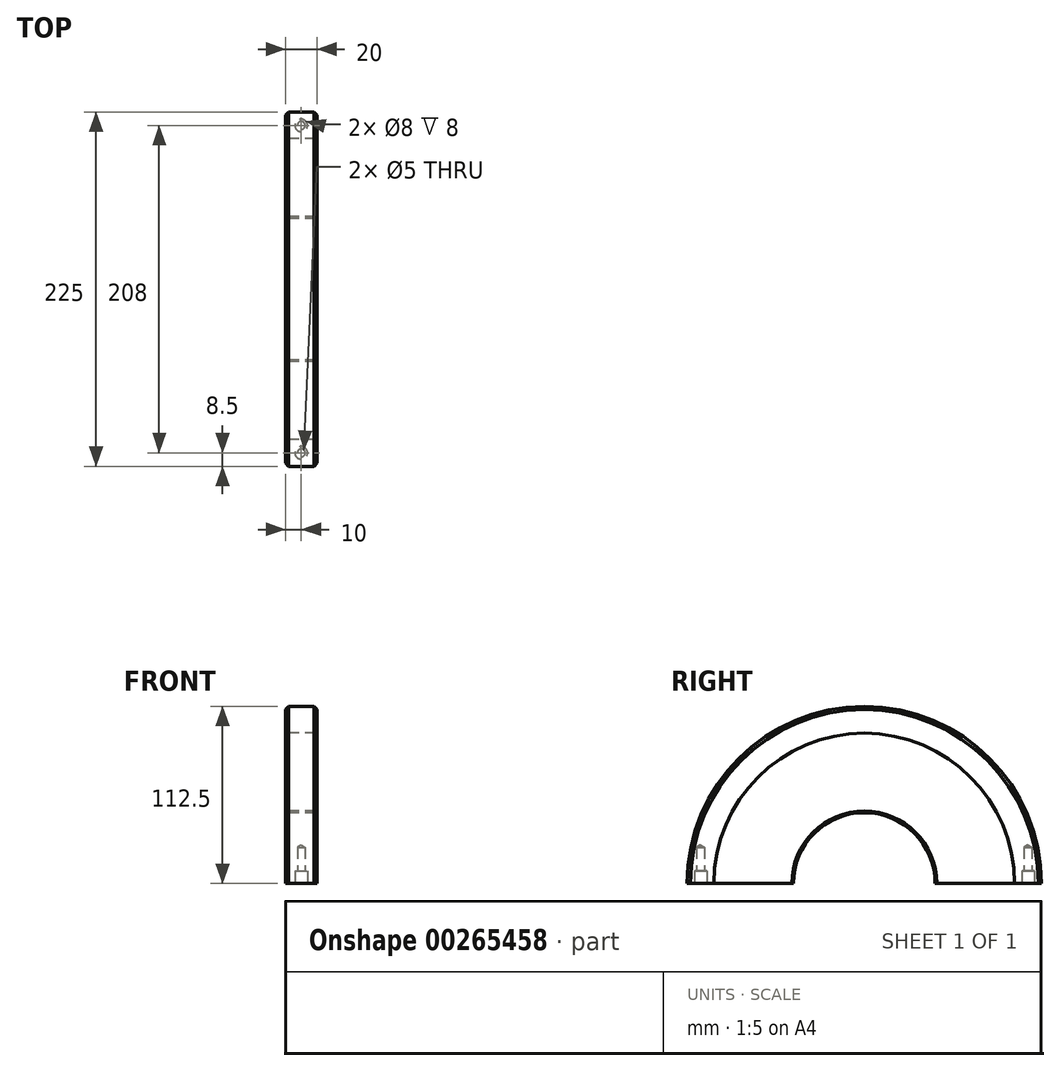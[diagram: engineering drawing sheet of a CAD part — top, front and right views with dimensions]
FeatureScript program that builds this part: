
annotation { "Feature Type Name" : "Feature", "Feature Type Description" : "" }
export const myFeature = defineFeature(function(context is Context, id is Id, definition is map)
    precondition{}
    {
        {
            var Q0;
            Q0=qCreatedBy(makeId("Front.planeOp"),FACE);
            var sketch = newSketch(context, id + "F0", { "sketchPlane" : qUnion([Q0])});
            skLineSegment(sketch, "E0", {"start": v(-48.97, 0) * mm, "end": v(48.97, 0) * mm, "construction": true});
            skLineSegment(sketch, "E1.bottom", {"start": v(-10, 46) * mm, "end": v(10, 46) * mm});
            skLineSegment(sketch, "E1.top", {"start": v(-10, 45) * mm, "end": v(10, 45) * mm});
            skLineSegment(sketch, "E1.left", {"start": v(-10, 46) * mm, "end": v(-10, 45) * mm});
            skLineSegment(sketch, "E1.right", {"start": v(10, 46) * mm, "end": v(10, 45) * mm});
            skLineSegment(sketch, "E2", {"start": v(0, 12.38) * mm, "end": v(0, -12.38) * mm, "construction": true});
            skSolve(sketch);
        }
        {
            var Q0;
            Q0=makeQuery(id+"F0.imprint","IMPRINT",FACE,{"disambiguationData":[TD([[makeQuery(id+"F0.imprint","IMPRINT",EDGE,{"derivedFrom":sQuery(id+"F0.wireOp",EDGE,"E1.bottom")}),-1.0]])]});
            var Q1;
            Q1=sQuery(id+"F0.wireOp",EDGE,"E0");
            revolve(context, id + "F1", {"entities" : qUnion([Q0]), "axis" : qUnion([Q1]), "revolveType" : RevolveType.FULL});
        }
        {
            var Q0;
            Q0=qCreatedBy(makeId("Front.planeOp"),FACE);
            var sketch = newSketch(context, id + "F2", { "sketchPlane" : qUnion([Q0])});
            skLineSegment(sketch, "E3.bottom", {"start": v(-10, 95.5) * mm, "end": v(10, 95.5) * mm});
            skLineSegment(sketch, "E3.top", {"start": v(-10, 46) * mm, "end": v(10, 46) * mm});
            skLineSegment(sketch, "E3.left", {"start": v(-10, 95.5) * mm, "end": v(-10, 46) * mm});
            skLineSegment(sketch, "E3.right", {"start": v(10, 95.5) * mm, "end": v(10, 46) * mm});
            skLineSegment(sketch, "E4", {"start": v(-46.04, 0) * mm, "end": v(46.04, 0) * mm, "construction": true});
            skSolve(sketch);
        }
        {
            var Q0;
            Q0=makeQuery(id+"F2.imprint","IMPRINT",FACE,{"disambiguationData":[TD([[makeQuery(id+"F2.imprint","IMPRINT",EDGE,{"derivedFrom":sQuery(id+"F2.wireOp",EDGE,"E3.bottom")}),-1.0]])]});
            var Q1;
            Q1=sQuery(id+"F2.wireOp",EDGE,"E4");
            revolve(context, id + "F3", {"entities" : qUnion([Q0]), "axis" : qUnion([Q1]), "revolveType" : RevolveType.FULL});
        }
        {
            var Q0;
            Q0=qCreatedBy(makeId("Front.planeOp"),FACE);
            var sketch = newSketch(context, id + "F4", { "sketchPlane" : qUnion([Q0])});
            skLineSegment(sketch, "E5", {"start": v(-40.4, 0) * mm, "end": v(40.4, 0) * mm, "construction": true});
            skLineSegment(sketch, "E6.bottom", {"start": v(-10, 112.5) * mm, "end": v(10, 112.5) * mm});
            skLineSegment(sketch, "E6.top", {"start": v(-10, 95.5) * mm, "end": v(10, 95.5) * mm});
            skLineSegment(sketch, "E6.left", {"start": v(-10, 112.5) * mm, "end": v(-10, 95.5) * mm});
            skLineSegment(sketch, "E6.right", {"start": v(10, 112.5) * mm, "end": v(10, 95.5) * mm});
            skSolve(sketch);
        }
        {
            var Q0;
            Q0=makeQuery(id+"F4.imprint","IMPRINT",FACE,{"disambiguationData":[TD([[makeQuery(id+"F4.imprint","IMPRINT",EDGE,{"derivedFrom":sQuery(id+"F4.wireOp",EDGE,"E6.bottom")}),-1.0]])]});
            var Q1;
            Q1=sQuery(id+"F4.wireOp",EDGE,"E5");
            revolve(context, id + "F5", {"entities" : qUnion([Q0]), "axis" : qUnion([Q1]), "revolveType" : RevolveType.FULL});
        }
        {
            var Q0;
            Q0=qCreatedBy(makeId("Right.planeOp"),FACE);
            var sketch = newSketch(context, id + "F6", { "sketchPlane" : qUnion([Q0])});
            skLineSegment(sketch, "E7", {"start": v(-50, 95.16) * mm, "end": v(-50, 125.78) * mm});
            skLineSegment(sketch, "E8", {"start": v(-30, 145.78) * mm, "end": v(30, 145.78) * mm});
            skLineSegment(sketch, "E9", {"start": v(50, 125.78) * mm, "end": v(50, 95.16) * mm});
            skPoint(sketch, "E10.visualSharp", {"position": v(50, 145.78) * mm});
            skArc(sketch, "E10.filletArc", {"start": v(50, 125.78) * mm, "mid": v(44.14, 139.92) * mm, "end": v(30, 145.78) * mm});
            skPoint(sketch, "E11.visualSharp", {"position": v(-50, 145.78) * mm});
            skArc(sketch, "E11.filletArc", {"start": v(-30, 145.78) * mm, "mid": v(-44.14, 139.92) * mm, "end": v(-50, 125.78) * mm});
            skPoint(sketch, "E12", {"position": v(50, 100.78) * mm});
            skSolve(sketch);
        }
        {
            var Q0;
            Q0=qCreatedBy(makeId("Top.planeOp"),FACE);
            var Q1;
            Q1=sQuery(id+"F6.wireOp",VERTEX,"E7.start");
            cPlane(context, id + "F7", {"entities" : qUnion([Q0, Q1]), "cplaneType" : CPlaneType.PLANE_POINT, "offset" : 25 * mm, "width" : 150 * mm, "height" : 150 * mm});
        }
        {
            var Q0;
            Q0=makeQuery(id+"F5.opRevolve","SWEPT_EDGE",EDGE,{"disambiguationData":[OSD([sQuery(id+"F4.wireOp",EDGE,"E6.bottom"),sQuery(id+"F4.wireOp",EDGE,"E6.right")])]});
            var Q1;
            Q1=makeQuery(id+"F5.opRevolve","SWEPT_EDGE",EDGE,{"disambiguationData":[OSD([sQuery(id+"F4.wireOp",EDGE,"E6.bottom"),sQuery(id+"F4.wireOp",EDGE,"E6.left")])]});
            chamfer(context, id + "F8", {"entities" : qUnion([Q0, Q1]), "width" : 2 * mm, "tangentPropagation" : true});
        }
        {
            var Q0;
            Q0=qCreatedBy(makeId("Front.planeOp"),FACE);
            var sketch = newSketch(context, id + "F9", { "sketchPlane" : qUnion([Q0])});
            skLineSegment(sketch, "E13.bottom", {"start": v(-10, 0) * mm, "end": v(10, 0) * mm});
            skLineSegment(sketch, "E13.top", {"start": v(-10, -115) * mm, "end": v(10, -115) * mm});
            skLineSegment(sketch, "E13.left", {"start": v(-10, 0) * mm, "end": v(-10, -115) * mm});
            skLineSegment(sketch, "E13.right", {"start": v(10, 0) * mm, "end": v(10, -115) * mm});
            skSolve(sketch);
        }
        {
            var Q0;
            Q0=qSketchRegion(id+"F9",true);
            extrude(context, id + "F10", {"entities" : qUnion([Q0]), "operationType" : NewBodyOperationType.REMOVE, "endBound" : BoundingType.THROUGH_ALL, "depth" : 25 * mm, "hasSecondDirection" : true, "secondDirectionBound" : SecondDirectionBoundingType.THROUGH_ALL, "secondDirectionOppositeDirection" : true, "secondDirectionDepth" : 25 * mm});
        }
        {
            var Q0;
            {var subQ0=sQuery(id+"F4.wireOp",EDGE,"E6.right");var subQ1=sQuery(id+"F4.wireOp",EDGE,"E6.left");var subQ2=sQuery(id+"F4.wireOp",EDGE,"E6.bottom");Q0=makeQuery(id+"F10.boolean.opBoolean","COPY",FACE,{"disambiguationData":[TD([makeQuery(id+"F5.opRevolve","SWEPT_FACE",FACE,{"disambiguationData":[OSD([subQ2])]}),makeQuery(id+"F5.opRevolve","SWEPT_FACE",FACE,{"disambiguationData":[OSD([sQuery(id+"F4.wireOp",EDGE,"E6.top")])]}),makeQuery(id+"F5.opRevolve","SWEPT_FACE",FACE,{"disambiguationData":[OSD([subQ1])]}),makeQuery(id+"F5.opRevolve","SWEPT_FACE",FACE,{"disambiguationData":[OSD([subQ0])]}),makeQuery(id+"F8.opChamfer","BLEND_FACE",FACE,{"disambiguationData":[OSD([subQ2,subQ1])]}),makeQuery(id+"F8.opChamfer","BLEND_FACE",FACE,{"disambiguationData":[OSD([subQ2,subQ0])]})]),OD(0.0)],"derivedFrom":makeQuery(id+"F10.opExtrude","SWEPT_FACE",FACE,{"disambiguationData":[OSD([sQuery(id+"F9.wireOp",EDGE,"E13.bottom")])]})});}
            var sketch = newSketch(context, id + "F11", { "sketchPlane" : qUnion([Q0])});
            skCircle(sketch, "E14", {"center": v(0, 104) * mm, "radius": 4 * mm});
            skLineSegment(sketch, "E15", {"start": v(0, 112.5) * mm, "end": v(0, 95.5) * mm, "construction": true});
            skPoint(sketch, "E16.MirrorP", {"position": v(0, -104) * mm});
            skCircle(sketch, "E17.MirrorC", {"center": v(0, -104) * mm, "radius": 4 * mm});
            skSolve(sketch);
        }
        {
            var Q0;
            Q0 = qSketchRegion(id + "F11", true);
            extrude(context, id + "F12", {"entities" : qUnion([Q0]), "operationType" : NewBodyOperationType.REMOVE, "oppositeDirection" : true, "depth" : 8 * mm});
        }
        {
            var Q0;
            Q0=makeQuery(id+"F12.boolean.opBoolean","COPY",FACE,{"derivedFrom":makeQuery(id+"F12.opExtrude","CAP_FACE",FACE,{"disambiguationData":[OSD([sQuery(id+"F11.wireOp",EDGE,"E14")])],"isStart":false})});
            var sketch = newSketch(context, id + "F13", { "sketchPlane" : qUnion([Q0])});
            skPoint(sketch, "E18.0", {"position": v(0, 104) * mm});
            skPoint(sketch, "E18.1", {"position": v(0, -104) * mm});
            skSolve(sketch);
        }
        {
            var Q0;
            Q0=sQuery(id+"F13.wireOp",VERTEX,"E18.0");
            var Q1;
            Q1=sQuery(id+"F13.wireOp",VERTEX,"E18.1");
            var Q2;
            Q2=makeQuery(id+"F5.opRevolve","SWEPT_BODY",BODY,{"disambiguationData":[OSD([sQuery(id+"F4.wireOp",EDGE,"E6.bottom"),sQuery(id+"F4.wireOp",EDGE,"E6.top"),sQuery(id+"F4.wireOp",EDGE,"E6.left"),sQuery(id+"F4.wireOp",EDGE,"E6.right")])]});
            hole(context, id + "F14", {"style" : HoleStyle.SIMPLE, "endStyle" : HoleEndStyle.BLIND, "standardTappedOrClearance" : lookupTablePath({ "standard" : "ISO", "engagement" : "75%", "pitch" : "1 mm", "size" : "M6", "type" : "Tapped" }), "standardBlindInLast" : lookupTablePath({ "standard" : "ISO", "engagement" : "75%", "pitch" : "1 mm", "size" : "M6", "type" : "Tapped" }), "holeDiameter" : 5 * mm, "showTappedDepth" : true, "holeDepth" : 15 * mm, "tappedDepth" : 12 * mm, "tapClearance" : 3, "locations" : qUnion([Q0, Q1]), "scope" : qUnion([Q2]), "majorDiameter" : 6 * mm});
        }
    });
